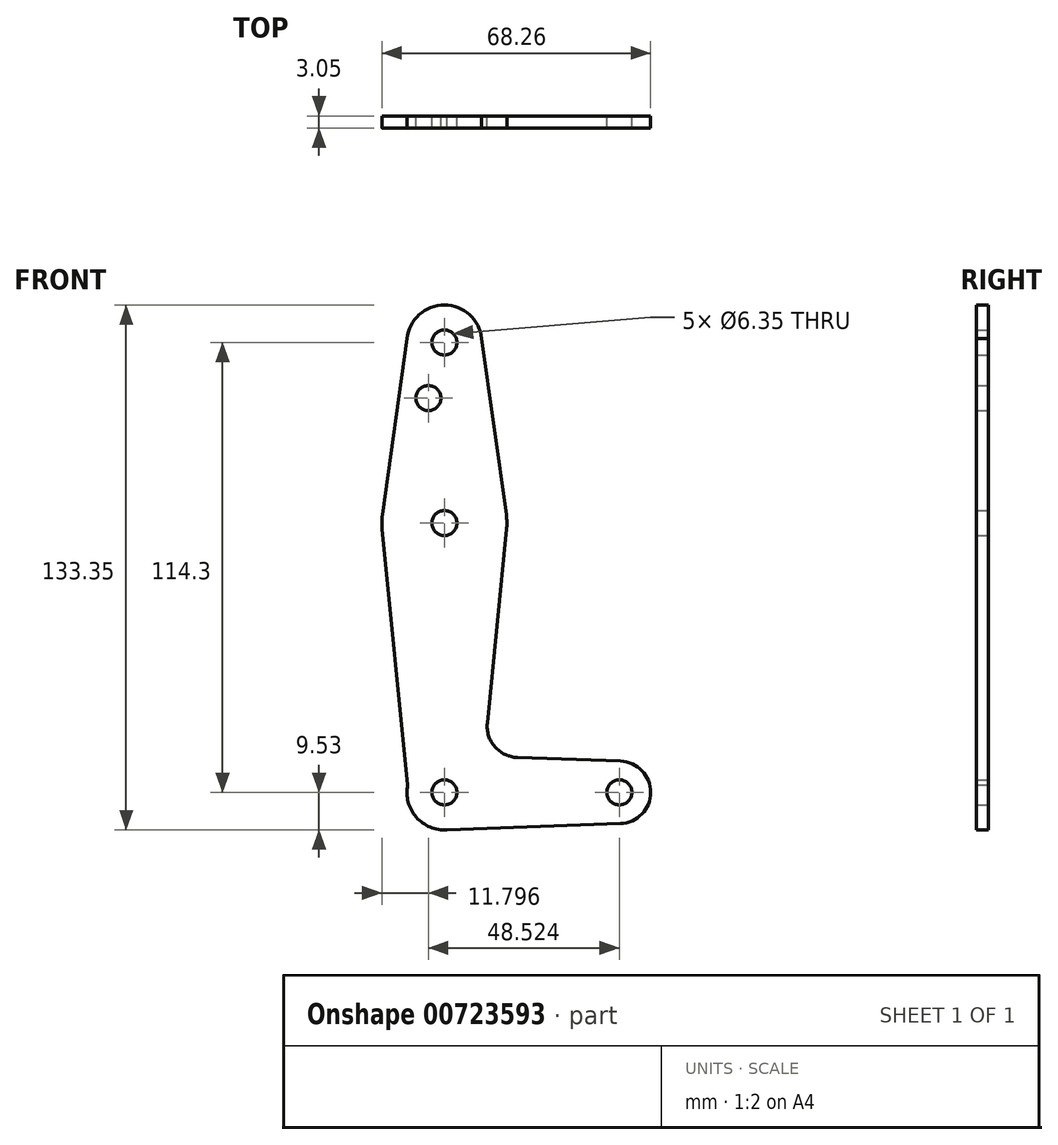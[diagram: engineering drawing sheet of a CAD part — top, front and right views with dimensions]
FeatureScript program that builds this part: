
annotation { "Feature Type Name" : "Feature", "Feature Type Description" : "" }
export const myFeature = defineFeature(function(context is Context, id is Id, definition is map)
    precondition{}
    {
        {
            var Q0;
            Q0=qCreatedBy(makeId("Front.planeOp"),FACE);
            var sketch = newSketch(context, id + "F0", { "sketchPlane" : qUnion([Q0])});
            skLineSegment(sketch, "E0", {"start": v(0, 0) * mm, "end": v(0, 114.3) * mm, "construction": true});
            skLineSegment(sketch, "E1", {"start": v(0, 0) * mm, "end": v(44.45, 0) * mm, "construction": true});
            skCircle(sketch, "E2", {"center": v(0, 114.3) * mm, "radius": 9.53 * mm});
            skCircle(sketch, "E3", {"center": v(0, 68.43) * mm, "radius": 15.88 * mm});
            skCircle(sketch, "E4", {"center": v(0, 0) * mm, "radius": 9.53 * mm});
            skCircle(sketch, "E5", {"center": v(44.45, 0) * mm, "radius": 7.94 * mm});
            skLineSegment(sketch, "E6", {"start": v(-9.37, 115.99) * mm, "end": v(-15.72, 70.63) * mm});
            skLineSegment(sketch, "E7", {"start": v(-15.8, 66.86) * mm, "end": v(-9.33, 1.9) * mm});
            skLineSegment(sketch, "E8", {"start": v(9.37, 115.99) * mm, "end": v(15.72, 70.63) * mm});
            skLineSegment(sketch, "E9", {"start": v(15.8, 66.86) * mm, "end": v(10.9, 17.6) * mm});
            skLineSegment(sketch, "E10", {"start": v(18.52, 8.87) * mm, "end": v(44.73, 7.93) * mm});
            skLineSegment(sketch, "E11", {"start": v(0, -9.53) * mm, "end": v(44.73, -7.93) * mm});
            skCircle(sketch, "E12", {"center": v(0, 114.3) * mm, "radius": 3.18 * mm});
            skCircle(sketch, "E13", {"center": v(0, 68.43) * mm, "radius": 3.18 * mm});
            skCircle(sketch, "E14", {"center": v(0, 0) * mm, "radius": 3.18 * mm});
            skCircle(sketch, "E15", {"center": v(44.45, 0) * mm, "radius": 3.18 * mm});
            skCircle(sketch, "E16", {"center": v(-4.07, 100.17) * mm, "radius": 3.18 * mm});
            skPoint(sketch, "E17.newPointA", {"position": v(9.33, 1.9) * mm});
            skArc(sketch, "E17.filletArc", {"start": v(10.9, 17.6) * mm, "mid": v(12.82, 11.58) * mm, "end": v(18.52, 8.87) * mm});
            skSolve(sketch);
        }
        {
            var Q0;
            Q0 = qSketchRegion(id + "F0", true);
            extrude(context, id + "F1", {"entities" : qUnion([Q0]), "depth" : 3.05 * mm, "offsetDistance" : 25.4 * mm});
        }
    });
